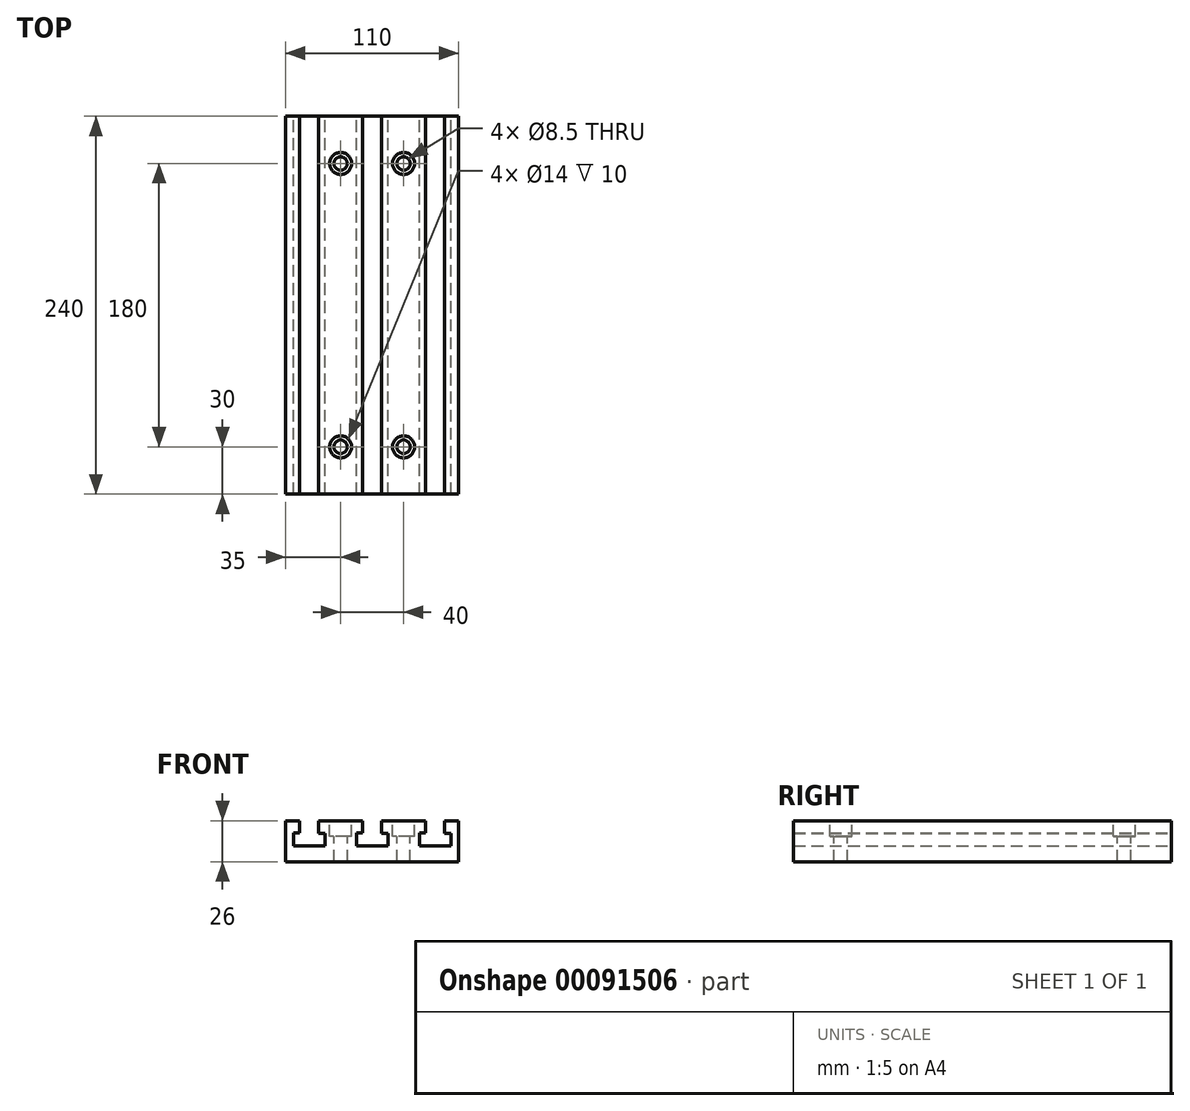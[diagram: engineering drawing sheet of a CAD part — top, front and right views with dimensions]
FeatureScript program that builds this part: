
annotation { "Feature Type Name" : "Feature", "Feature Type Description" : "" }
export const myFeature = defineFeature(function(context is Context, id is Id, definition is map)
    precondition{}
    {
        {
            var Q0;
            Q0=qCreatedBy(makeId("Front.planeOp"),FACE);
            var sketch = newSketch(context, id + "F0", { "sketchPlane" : qUnion([Q0])});
            skLineSegment(sketch, "E0.bottom", {"start": v(-55, 0) * mm, "end": v(55, 0) * mm});
            skLineSegment(sketch, "E0.top", {"start": v(-55, 26) * mm, "end": v(-46, 26) * mm});
            skLineSegment(sketch, "E0.left", {"start": v(-55, 0) * mm, "end": v(-55, 26) * mm});
            skLineSegment(sketch, "E0.right", {"start": v(55, 0) * mm, "end": v(55, 26) * mm});
            skLineSegment(sketch, "E1", {"start": v(-46, 26) * mm, "end": v(-46, 18.2) * mm});
            skLineSegment(sketch, "E2", {"start": v(-46, 18.2) * mm, "end": v(-50, 18.2) * mm});
            skLineSegment(sketch, "E3", {"start": v(-50, 18.2) * mm, "end": v(-50, 10) * mm});
            skLineSegment(sketch, "E4", {"start": v(-50, 10) * mm, "end": v(-30, 10) * mm});
            skLineSegment(sketch, "E5", {"start": v(-30, 10) * mm, "end": v(-30, 18) * mm});
            skLineSegment(sketch, "E6", {"start": v(-30, 18) * mm, "end": v(-34, 18) * mm});
            skLineSegment(sketch, "E7", {"start": v(-34, 18) * mm, "end": v(-34, 26) * mm});
            skLineSegment(sketch, "E8.trimOffspring", {"start": v(-34, 26) * mm, "end": v(-6, 26) * mm});
            skLineSegment(sketch, "E9.1.0.0", {"start": v(6, 18) * mm, "end": v(6, 26) * mm});
            skLineSegment(sketch, "E9.1.0.1", {"start": v(10, 18) * mm, "end": v(6, 18) * mm});
            skLineSegment(sketch, "E9.1.0.2", {"start": v(10, 10) * mm, "end": v(10, 18) * mm});
            skLineSegment(sketch, "E9.1.0.3", {"start": v(-10, 10) * mm, "end": v(10, 10) * mm});
            skLineSegment(sketch, "E9.1.0.4", {"start": v(-10, 18.2) * mm, "end": v(-10, 10) * mm});
            skLineSegment(sketch, "E9.1.0.5", {"start": v(-6, 18.2) * mm, "end": v(-10, 18.2) * mm});
            skLineSegment(sketch, "E9.1.0.6", {"start": v(-6, 26) * mm, "end": v(-6, 18.2) * mm});
            skLineSegment(sketch, "E9.2.0.0", {"start": v(46, 18) * mm, "end": v(46, 26) * mm});
            skLineSegment(sketch, "E9.2.0.1", {"start": v(50, 18) * mm, "end": v(46, 18) * mm});
            skLineSegment(sketch, "E9.2.0.2", {"start": v(50, 10) * mm, "end": v(50, 18) * mm});
            skLineSegment(sketch, "E9.2.0.3", {"start": v(30, 10) * mm, "end": v(50, 10) * mm});
            skLineSegment(sketch, "E9.2.0.4", {"start": v(30, 18.2) * mm, "end": v(30, 10) * mm});
            skLineSegment(sketch, "E9.2.0.5", {"start": v(34, 18.2) * mm, "end": v(30, 18.2) * mm});
            skLineSegment(sketch, "E9.2.0.6", {"start": v(34, 26) * mm, "end": v(34, 18.2) * mm});
            skLineSegment(sketch, "E9.direction1", {"start": v(-34, 18) * mm, "end": v(6, 18) * mm, "construction": true});
            skLineSegment(sketch, "E10.trimOffspring", {"start": v(6, 26) * mm, "end": v(34, 26) * mm});
            skLineSegment(sketch, "E11.trimOffspring", {"start": v(46, 26) * mm, "end": v(55, 26) * mm});
            skSolve(sketch);
        }
        {
            var Q0;
            Q0=makeQuery(id+"F0.imprint","IMPRINT",FACE,{"disambiguationData":[TD([[makeQuery(id+"F0.imprint","IMPRINT",EDGE,{"derivedFrom":sQuery(id+"F0.wireOp",EDGE,"E0.bottom")}),1.0]])]});
            extrude(context, id + "F1", {"entities" : qUnion([Q0]), "endBound" : BoundingType.SYMMETRIC, "depth" : 240 * mm});
        }
        {
            var Q0;
            Q0=makeQuery(id+"F1.opExtrude","SWEPT_FACE",FACE,{"disambiguationData":[OSD([sQuery(id+"F0.wireOp",EDGE,"E8.trimOffspring")])]});
            var sketch = newSketch(context, id + "F2", { "sketchPlane" : qUnion([Q0])});
            skPoint(sketch, "E12", {"position": v(-20, -90) * mm});
            skPoint(sketch, "E13", {"position": v(20, -90) * mm});
            skPoint(sketch, "E14", {"position": v(-20, 90) * mm});
            skPoint(sketch, "E15", {"position": v(20, 90) * mm});
            skSolve(sketch);
        }
        {
            var Q0;
            Q0=sQuery(id+"F2.wireOp",VERTEX,"E12");
            var Q1;
            Q1=sQuery(id+"F2.wireOp",VERTEX,"E13");
            var Q2;
            Q2=sQuery(id+"F2.wireOp",VERTEX,"E14");
            var Q3;
            Q3=sQuery(id+"F2.wireOp",VERTEX,"E15");
            var Q4;
            Q4=makeQuery(id+"F1.opExtrude","SWEPT_BODY",BODY,{"disambiguationData":[OSD([sQuery(id+"F0.wireOp",EDGE,"E0.bottom"),sQuery(id+"F0.wireOp",EDGE,"E0.top"),sQuery(id+"F0.wireOp",EDGE,"E0.left"),sQuery(id+"F0.wireOp",EDGE,"E0.right"),sQuery(id+"F0.wireOp",EDGE,"E1"),sQuery(id+"F0.wireOp",EDGE,"E2"),sQuery(id+"F0.wireOp",EDGE,"E3"),sQuery(id+"F0.wireOp",EDGE,"E4"),sQuery(id+"F0.wireOp",EDGE,"E5"),sQuery(id+"F0.wireOp",EDGE,"E6"),sQuery(id+"F0.wireOp",EDGE,"E7"),sQuery(id+"F0.wireOp",EDGE,"E8.trimOffspring"),sQuery(id+"F0.wireOp",EDGE,"E9.1.0.0"),sQuery(id+"F0.wireOp",EDGE,"E9.1.0.1"),sQuery(id+"F0.wireOp",EDGE,"E9.1.0.2"),sQuery(id+"F0.wireOp",EDGE,"E9.1.0.3"),sQuery(id+"F0.wireOp",EDGE,"E9.1.0.4"),sQuery(id+"F0.wireOp",EDGE,"E9.1.0.5"),sQuery(id+"F0.wireOp",EDGE,"E9.1.0.6"),sQuery(id+"F0.wireOp",EDGE,"E9.2.0.0"),sQuery(id+"F0.wireOp",EDGE,"E9.2.0.1"),sQuery(id+"F0.wireOp",EDGE,"E9.2.0.2"),sQuery(id+"F0.wireOp",EDGE,"E9.2.0.3"),sQuery(id+"F0.wireOp",EDGE,"E9.2.0.4"),sQuery(id+"F0.wireOp",EDGE,"E9.2.0.5"),sQuery(id+"F0.wireOp",EDGE,"E9.2.0.6"),sQuery(id+"F0.wireOp",EDGE,"E10.trimOffspring"),sQuery(id+"F0.wireOp",EDGE,"E11.trimOffspring")])]});
            hole(context, id + "F3", {"style" : HoleStyle.C_BORE, "endStyle" : HoleEndStyle.THROUGH, "holeDiameter" : 8.5 * mm, "cBoreDiameter" : 14 * mm, "cBoreDepth" : 10 * mm, "startFromSketch" : true, "locations" : qUnion([Q0, Q1, Q2, Q3]), "scope" : qUnion([Q4]), "isTappedThrough" : true});
        }
        {
            var Q0;
            Q0=makeQuery(id+"F1.opExtrude","SWEPT_BODY",BODY,{"disambiguationData":[OSD([sQuery(id+"F0.wireOp",EDGE,"E0.bottom"),sQuery(id+"F0.wireOp",EDGE,"E0.top"),sQuery(id+"F0.wireOp",EDGE,"E0.left"),sQuery(id+"F0.wireOp",EDGE,"E0.right"),sQuery(id+"F0.wireOp",EDGE,"E1"),sQuery(id+"F0.wireOp",EDGE,"E2"),sQuery(id+"F0.wireOp",EDGE,"E3"),sQuery(id+"F0.wireOp",EDGE,"E4"),sQuery(id+"F0.wireOp",EDGE,"E5"),sQuery(id+"F0.wireOp",EDGE,"E6"),sQuery(id+"F0.wireOp",EDGE,"E7"),sQuery(id+"F0.wireOp",EDGE,"E8.trimOffspring"),sQuery(id+"F0.wireOp",EDGE,"E9.1.0.0"),sQuery(id+"F0.wireOp",EDGE,"E9.1.0.1"),sQuery(id+"F0.wireOp",EDGE,"E9.1.0.2"),sQuery(id+"F0.wireOp",EDGE,"E9.1.0.3"),sQuery(id+"F0.wireOp",EDGE,"E9.1.0.4"),sQuery(id+"F0.wireOp",EDGE,"E9.1.0.5"),sQuery(id+"F0.wireOp",EDGE,"E9.1.0.6"),sQuery(id+"F0.wireOp",EDGE,"E9.2.0.0"),sQuery(id+"F0.wireOp",EDGE,"E9.2.0.1"),sQuery(id+"F0.wireOp",EDGE,"E9.2.0.2"),sQuery(id+"F0.wireOp",EDGE,"E9.2.0.3"),sQuery(id+"F0.wireOp",EDGE,"E9.2.0.4"),sQuery(id+"F0.wireOp",EDGE,"E9.2.0.5"),sQuery(id+"F0.wireOp",EDGE,"E9.2.0.6"),sQuery(id+"F0.wireOp",EDGE,"E10.trimOffspring"),sQuery(id+"F0.wireOp",EDGE,"E11.trimOffspring")])]});
            transform(context, id + "F4", {"entities" : qUnion([Q0]), "transformType" : TransformType.TRANSLATION_3D, "dx" : 0 * mm, "dy" : 0 * mm, "dz" : 0 * mm, "makeCopy" : true});
        }
        {
            var Q0;
            Q0=makeQuery(id+"F4.opPattern","COPY",BODY,{"derivedFrom":makeQuery(id+"F1.opExtrude","SWEPT_BODY",BODY,{"disambiguationData":[OSD([sQuery(id+"F0.wireOp",EDGE,"E0.bottom"),sQuery(id+"F0.wireOp",EDGE,"E0.top"),sQuery(id+"F0.wireOp",EDGE,"E0.left"),sQuery(id+"F0.wireOp",EDGE,"E0.right"),sQuery(id+"F0.wireOp",EDGE,"E1"),sQuery(id+"F0.wireOp",EDGE,"E2"),sQuery(id+"F0.wireOp",EDGE,"E3"),sQuery(id+"F0.wireOp",EDGE,"E4"),sQuery(id+"F0.wireOp",EDGE,"E5"),sQuery(id+"F0.wireOp",EDGE,"E6"),sQuery(id+"F0.wireOp",EDGE,"E7"),sQuery(id+"F0.wireOp",EDGE,"E8.trimOffspring"),sQuery(id+"F0.wireOp",EDGE,"E9.1.0.0"),sQuery(id+"F0.wireOp",EDGE,"E9.1.0.1"),sQuery(id+"F0.wireOp",EDGE,"E9.1.0.2"),sQuery(id+"F0.wireOp",EDGE,"E9.1.0.3"),sQuery(id+"F0.wireOp",EDGE,"E9.1.0.4"),sQuery(id+"F0.wireOp",EDGE,"E9.1.0.5"),sQuery(id+"F0.wireOp",EDGE,"E9.1.0.6"),sQuery(id+"F0.wireOp",EDGE,"E9.2.0.0"),sQuery(id+"F0.wireOp",EDGE,"E9.2.0.1"),sQuery(id+"F0.wireOp",EDGE,"E9.2.0.2"),sQuery(id+"F0.wireOp",EDGE,"E9.2.0.3"),sQuery(id+"F0.wireOp",EDGE,"E9.2.0.4"),sQuery(id+"F0.wireOp",EDGE,"E9.2.0.5"),sQuery(id+"F0.wireOp",EDGE,"E9.2.0.6"),sQuery(id+"F0.wireOp",EDGE,"E10.trimOffspring"),sQuery(id+"F0.wireOp",EDGE,"E11.trimOffspring")])]}),"instanceName":"1"});
            deleteBodies(context, id + "F5", {"entities" : qUnion([Q0])});
        }
    });
